# Revit family: xRail_System-Zoeller-(4_Inch)
name_source: partatom
category: Mechanical Equipment
revit_build: Autodesk Revit 2014 (Build: 20130308_1515(x64)
units: mm (PartAtom-declared; Revit-internal decimal feet)

## types (2) — shared parameters
Assembly Code = D2030400
Bracket Height = 60"
CW Connection = Yes
Connection Type = 4" Horizontal Flange
Default Elevation = 60"
Description = 4" Guide Rail System SS
HW Connection = No
Manufacturer = Zoeller
Material = Metal-Zoeller-Epoxy Powder Coated Ductile Iron
Model = 4" Rail System
Price = Prices may vary. Please consult Manufacturer Representative for most up-to-date price list.
Pump Discharge Diameter = 4"
Pump Discharge Radius = 2"
Rail System Discharge Diameter = 4"
Rail System Discharge Radius = 2"
URL = http://www.zoellerpumps.com
Vent Connection = No
Waste Connection = Yes

## per-type parameters (varying)
| type | Mounting Plate | Mounting Plate Material | Non-Sparking Rail System |
| 6039-0016 - 4" Rail System | Mounting_Plate-Zoeller-Rail_System-C00094 : C00094 - Mounting Plate | Metal-Zoeller-Powder Coated Cast Iron | No |
| 6039-0017 - 4" Non-Sparking Rail System | Mounting_Plate-Zoeller-Rail_System-C00095 : C00094 - Mounting Plate | Brass-Zoeller-Copper Alloy | Yes |

## geometry (parser evidence)
native form markers: Sweep x7
no freeform markers — native parametric forms only
